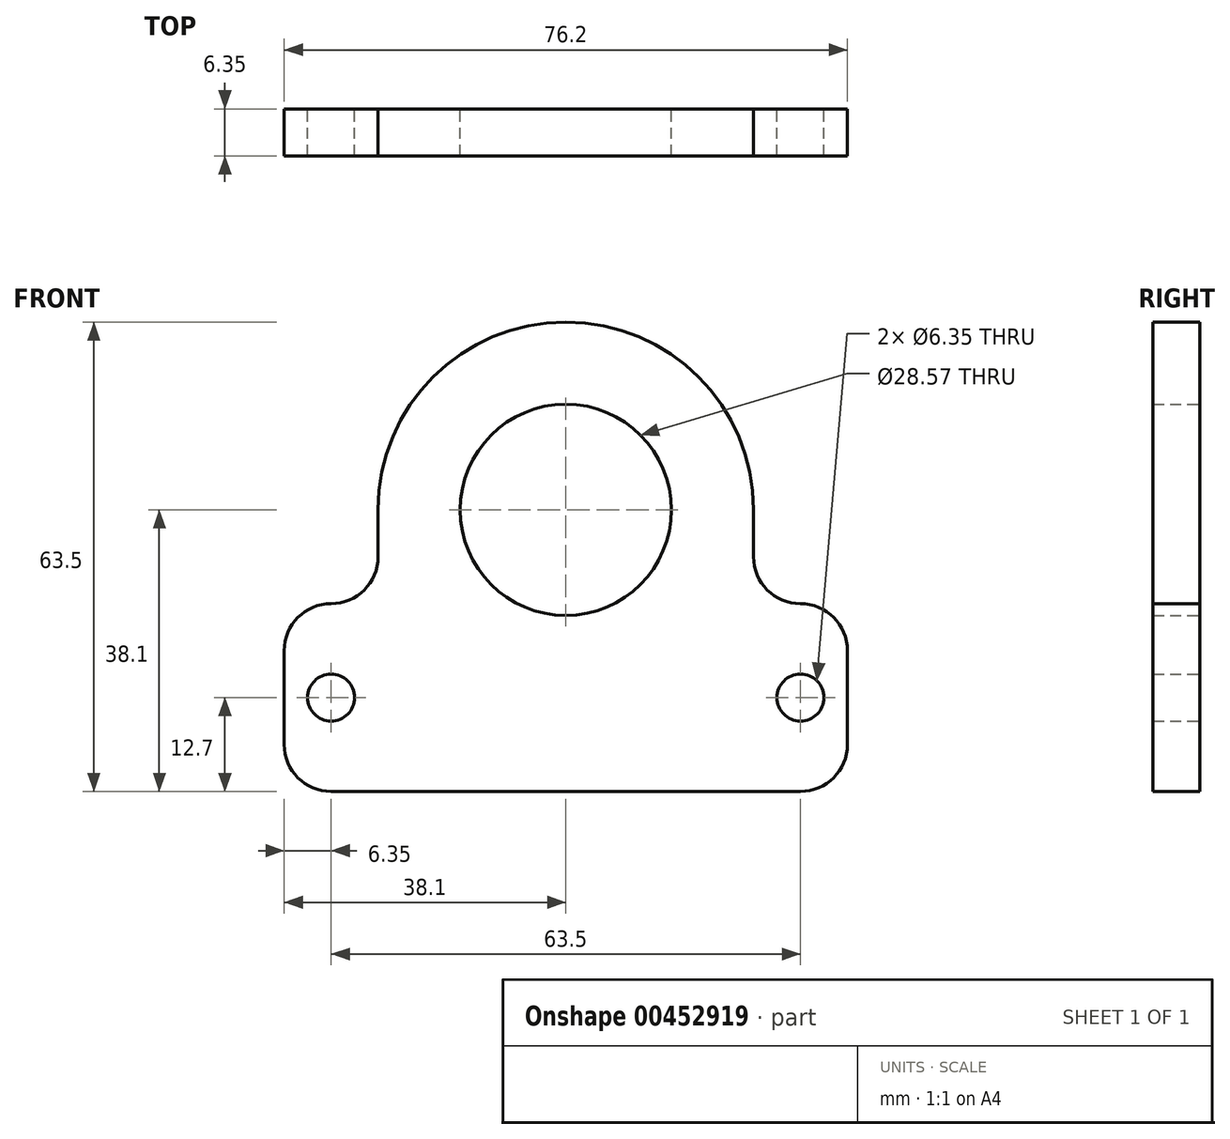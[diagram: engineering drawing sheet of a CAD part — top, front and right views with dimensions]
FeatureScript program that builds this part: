
annotation { "Feature Type Name" : "Feature", "Feature Type Description" : "" }
export const myFeature = defineFeature(function(context is Context, id is Id, definition is map)
    precondition{}
    {
        {
            var Q0;
            Q0=qCreatedBy(makeId("Front.planeOp"),FACE);
            var sketch = newSketch(context, id + "F0", { "sketchPlane" : qUnion([Q0])});
            skLineSegment(sketch, "E0.bottom", {"start": v(25.4, 0) * mm, "end": v(25.4, 0) * mm});
            skLineSegment(sketch, "E0.top", {"start": v(0, -63.5) * mm, "end": v(50.8, -63.5) * mm});
            skLineSegment(sketch, "E0.left", {"start": v(0, -25.4) * mm, "end": v(0, -31.75) * mm});
            skLineSegment(sketch, "E0.right", {"start": v(50.8, -25.4) * mm, "end": v(50.8, -31.75) * mm});
            skCircle(sketch, "E1", {"center": v(25.4, -25.4) * mm, "radius": 14.29 * mm});
            skCircle(sketch, "E2", {"center": v(-6.35, -50.8) * mm, "radius": 3.18 * mm});
            skCircle(sketch, "E3", {"center": v(57.15, -50.8) * mm, "radius": 3.18 * mm});
            skPoint(sketch, "E4.visualSharp", {"position": v(0, 0) * mm});
            skArc(sketch, "E4.filletArc", {"start": v(25.4, 0) * mm, "mid": v(7.44, -7.44) * mm, "end": v(0, -25.4) * mm});
            skPoint(sketch, "E5.visualSharp", {"position": v(50.8, 0) * mm});
            skArc(sketch, "E5.filletArc", {"start": v(50.8, -25.4) * mm, "mid": v(43.36, -7.44) * mm, "end": v(25.4, 0) * mm});
            skLineSegment(sketch, "E6.bottom", {"start": v(0, -63.5) * mm, "end": v(-6.35, -63.5) * mm});
            skLineSegment(sketch, "E6.top", {"start": v(-6.35, -38.1) * mm, "end": v(-6.35, -38.1) * mm});
            skLineSegment(sketch, "E6.left", {"start": v(0, -63.5) * mm, "end": v(0, -38.1) * mm});
            skLineSegment(sketch, "E6.right", {"start": v(-12.7, -57.15) * mm, "end": v(-12.7, -44.45) * mm});
            skLineSegment(sketch, "E7.bottom", {"start": v(50.8, -63.5) * mm, "end": v(57.15, -63.5) * mm});
            skLineSegment(sketch, "E7.top", {"start": v(57.15, -38.1) * mm, "end": v(57.15, -38.1) * mm});
            skLineSegment(sketch, "E7.left", {"start": v(50.8, -63.5) * mm, "end": v(50.8, -38.1) * mm});
            skLineSegment(sketch, "E7.right", {"start": v(63.5, -57.15) * mm, "end": v(63.5, -44.45) * mm});
            skPoint(sketch, "E8.visualSharp", {"position": v(-12.7, -38.1) * mm});
            skArc(sketch, "E8.filletArc", {"start": v(-6.35, -38.1) * mm, "mid": v(-10.84, -39.96) * mm, "end": v(-12.7, -44.45) * mm});
            skPoint(sketch, "E9.visualSharp", {"position": v(-12.7, -63.5) * mm});
            skArc(sketch, "E9.filletArc", {"start": v(-12.7, -57.15) * mm, "mid": v(-10.84, -61.64) * mm, "end": v(-6.35, -63.5) * mm});
            skPoint(sketch, "E10.visualSharp", {"position": v(63.5, -63.5) * mm});
            skArc(sketch, "E10.filletArc", {"start": v(57.15, -63.5) * mm, "mid": v(61.64, -61.64) * mm, "end": v(63.5, -57.15) * mm});
            skPoint(sketch, "E11.visualSharp", {"position": v(63.5, -38.1) * mm});
            skArc(sketch, "E11.filletArc", {"start": v(63.5, -44.45) * mm, "mid": v(61.64, -39.96) * mm, "end": v(57.15, -38.1) * mm});
            skArc(sketch, "E12.filletArc", {"start": v(-6.35, -38.1) * mm, "mid": v(-1.86, -36.24) * mm, "end": v(0, -31.75) * mm});
            skPoint(sketch, "E13.newPointA", {"position": v(50.8, -63.5) * mm});
            skArc(sketch, "E13.filletArc", {"start": v(50.8, -31.75) * mm, "mid": v(52.66, -36.24) * mm, "end": v(57.15, -38.1) * mm});
            skSolve(sketch);
        }
        {
            var Q0;
            Q0=qSketchRegion(id+"F0",true);
            extrude(context, id + "F1", {"entities" : qUnion([Q0]), "depth" : 6.35 * mm});
        }
    });
